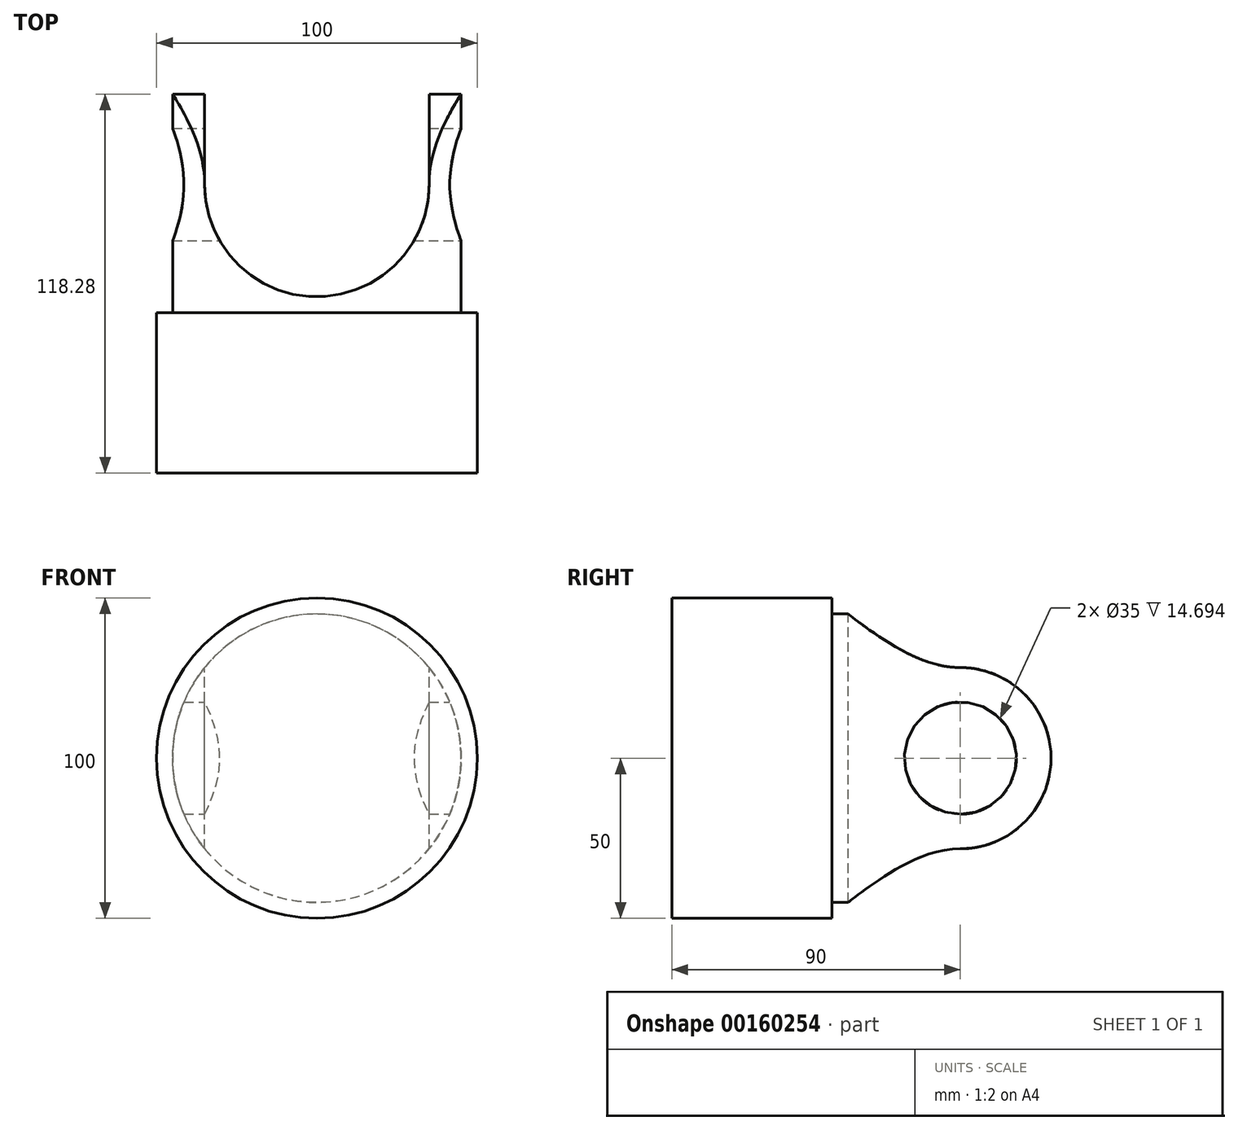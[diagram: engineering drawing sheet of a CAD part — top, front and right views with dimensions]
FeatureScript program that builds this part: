
annotation { "Feature Type Name" : "Feature", "Feature Type Description" : "" }
export const myFeature = defineFeature(function(context is Context, id is Id, definition is map)
    precondition{}
    {
        {
            var Q0;
            Q0=qCreatedBy(makeId("Front.planeOp"),FACE);
            var sketch = newSketch(context, id + "F0", { "sketchPlane" : qUnion([Q0])});
            skCircle(sketch, "E0", {"center": v(0, 0) * mm, "radius": 50 * mm});
            skSolve(sketch);
        }
        {
            var Q0;
            Q0=qSketchRegion(id+"F0",true);
            extrude(context, id + "F1", {"entities" : qUnion([Q0]), "oppositeDirection" : true, "depth" : 50 * mm});
        }
        {
            var Q0;
            Q0=makeQuery(id+"F1.opExtrude","CAP_FACE",FACE,{"disambiguationData":[OSD([sQuery(id+"F0.wireOp",EDGE,"E0")])],"isStart":false});
            var sketch = newSketch(context, id + "F2", { "sketchPlane" : qUnion([Q0])});
            skCircle(sketch, "E1", {"center": v(0, 0) * mm, "radius": 45 * mm});
            skSolve(sketch);
        }
        {
            var Q0;
            Q0=qSketchRegion(id+"F2",true);
            extrude(context, id + "F3", {"entities" : qUnion([Q0]), "operationType" : NewBodyOperationType.ADD, "depth" : 80 * mm});
        }
        {
            var Q0;
            Q0=qCreatedBy(makeId("Top.planeOp"),FACE);
            var sketch = newSketch(context, id + "F4", { "sketchPlane" : qUnion([Q0])});
            skCircle(sketch, "E2", {"center": v(0, 90) * mm, "radius": 35 * mm});
            skLineSegment(sketch, "E3", {"start": v(35, 90) * mm, "end": v(35, 130) * mm});
            skPoint(sketch, "E4", {"position": v(-35, 90) * mm});
            skLineSegment(sketch, "E5", {"start": v(-35, 90) * mm, "end": v(-35, 130) * mm});
            skLineSegment(sketch, "E6", {"start": v(-35, 130) * mm, "end": v(35, 130) * mm});
            skSolve(sketch);
        }
        {
            var Q0;
            Q0=qSketchRegion(id+"F4",true);
            extrude(context, id + "F5", {"entities" : qUnion([Q0]), "operationType" : NewBodyOperationType.REMOVE, "oppositeDirection" : true, "depth" : 200 * mm, "symmetric" : true});
        }
        {
            var Q0;
            Q0=makeQuery(id+"F5.boolean.opBoolean","COPY",FACE,{"derivedFrom":makeQuery(id+"F5.opExtrude","SWEPT_FACE",FACE,{"disambiguationData":[OSD([sQuery(id+"F4.wireOp",EDGE,"E5")])]})});
            var sketch = newSketch(context, id + "F6", { "sketchPlane" : qUnion([Q0])});
            skCircle(sketch, "E7", {"center": v(90, 0) * mm, "radius": 17.5 * mm});
            skArc(sketch, "E8", {"start": v(90, -28.28) * mm, "mid": v(118.28, 0) * mm, "end": v(90, 28.28) * mm});
            skLineSegment(sketch, "E9", {"start": v(90, 28.28) * mm, "end": v(130, 28.28) * mm});
            skLineSegment(sketch, "E10", {"start": v(130, 28.28) * mm, "end": v(130, -28.28) * mm});
            skLineSegment(sketch, "E11", {"start": v(130, -28.28) * mm, "end": v(90, -28.28) * mm});
            skSolve(sketch);
        }
        {
            var Q0;
            Q0=qSketchRegion(id+"F6",true);
            extrude(context, id + "F7", {"entities" : qUnion([Q0]), "operationType" : NewBodyOperationType.REMOVE, "oppositeDirection" : true, "depth" : 200 * mm, "symmetric" : true});
        }
    });
